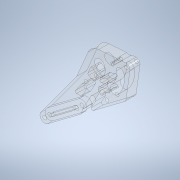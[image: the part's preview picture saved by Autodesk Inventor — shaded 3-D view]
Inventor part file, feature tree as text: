
AUTODESK INVENTOR PART (.ipt)
format: ipt  version: 2020.2 (Build 242310000, 310)  size: 931,328 bytes
history: native  units: mm
features: extrude x19, sketch x18, projected_geometry x15, fillet x4, other x3, hole x2
ambient origin geometry x8: Origin, YZ Plane, XZ Plane, XY Plane, X Axis, Y Axis, Z Axis, Center Point
bodies: Body1 (feature_tree)
feature tree (61):
  other  "ソリッド1"
  sketch  "スケッチ1"
  sketch  "スケッチ2"
  extrude  "押し出し1"  Depth=5.0mm TaperAngle=0.0deg
  hole  "穴1"  [1 undecoded]
  fillet  "フィレット1"  Radius=4.0mm
  extrude  "押し出し2"  Depth=5.0mm TaperAngle=0.0deg
  extrude  "押し出し3"  Depth=10.0mm TaperAngle=0.0deg
  extrude  "押し出し4"  Depth=1.0mm TaperAngle=0.0deg
  extrude  "押し出し5"  Depth=4.014257mm
  sketch  "スケッチ7"
  extrude  "押し出し6"  Depth=7.971681mm
  extrude  "押し出し7"  Depth=3.98584mm
  extrude  "押し出し8"  Depth=2.0mm TaperAngle=0.0deg
  extrude  "押し出し9"  Depth=4.0mm TaperAngle=0.0deg
  extrude  "押し出し10"  Depth=10.0mm TaperAngle=0.0deg
  extrude  "押し出し11"  Depth=2.0mm TaperAngle=0.0deg
  extrude  "押し出し12"  Depth=4.0mm TaperAngle=0.0deg
  sketch  "スケッチ12"
  extrude  "押し出し13"  Depth=2.0mm TaperAngle=0.0deg
  hole  "穴2"  [1 undecoded]
  extrude  "押し出し14"  Depth=6.5mm
  fillet  "フィレット2"  Radius=10.0mm
  extrude  "押し出し15"  Depth=16.0mm
  fillet  "フィレット3"  Radius=7.0mm
  extrude  "押し出し16"  Depth=8.0mm TaperAngle=0.0deg
  extrude  "押し出し17"  Depth=5.0mm
  fillet  "フィレット4"  Radius=5.0mm
  sketch  "スケッチ17"
  sketch  "スケッチ18"
  extrude  "押し出し18"  Depth=3.0mm
  extrude  "押し出し19"  Depth=3.0mm
  sketch  "スケッチ3"
  projected_geometry  "投影ループ1"
  sketch  "スケッチ4"
  projected_geometry  "投影ループ2"
  sketch  "スケッチ5"
  projected_geometry  "投影ループ3"
  sketch  "スケッチ6"
  projected_geometry  "投影ループ4"
  projected_geometry  "投影ループ5"
  sketch  "スケッチ8"
  projected_geometry  "投影ループ6"
  sketch  "スケッチ9"
  projected_geometry  "投影ループ7"
  sketch  "スケッチ10"
  projected_geometry  "投影ループ8"
  sketch  "スケッチ11"
  sketch  "スケッチ13"
  projected_geometry  "投影ループ9"
  sketch  "スケッチ14"
  projected_geometry  "投影ループ10"
  sketch  "スケッチ15"
  projected_geometry  "投影ループ11"
  sketch  "スケッチ16"
  projected_geometry  "投影ループ12"
  projected_geometry  "投影ループ13"
  projected_geometry  "投影ループ14"
  projected_geometry  "投影ループ15"
  other  "断面エッジを投影1"
  other  "断面エッジを投影2"
note: 2 required parameter values undecoded (feature->parameter linkage not recoverable at this tier; creation-order binding heuristic only, values carry confidence <= 0.55)
